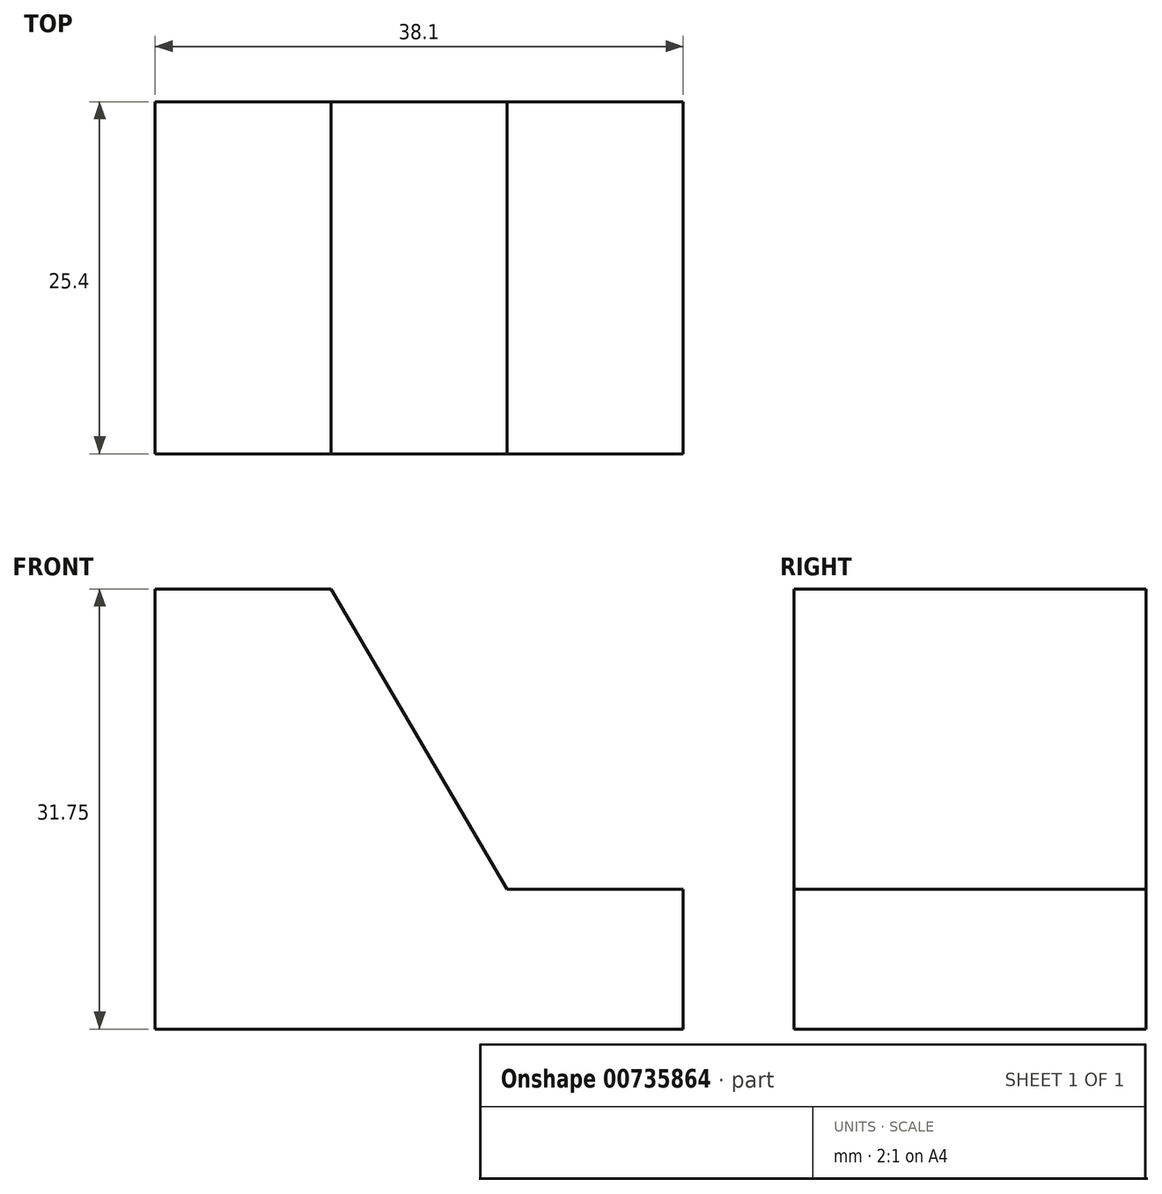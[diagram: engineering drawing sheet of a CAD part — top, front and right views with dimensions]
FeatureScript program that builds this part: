
annotation { "Feature Type Name" : "Feature", "Feature Type Description" : "" }
export const myFeature = defineFeature(function(context is Context, id is Id, definition is map)
    precondition{}
    {
        {
            var Q0;
            Q0=qCreatedBy(makeId("Front.planeOp"),FACE);
            var sketch = newSketch(context, id + "F0", { "sketchPlane" : qUnion([Q0])});
            skLineSegment(sketch, "E0", {"start": v(0, 0) * mm, "end": v(38.1, 0) * mm});
            skLineSegment(sketch, "E1", {"start": v(38.1, 0) * mm, "end": v(38.1, 31.75) * mm});
            skLineSegment(sketch, "E2", {"start": v(38.1, 31.75) * mm, "end": v(0, 31.75) * mm});
            skLineSegment(sketch, "E3", {"start": v(0, 31.75) * mm, "end": v(0, 0) * mm});
            skSolve(sketch);
        }
        {
            var Q0;
            Q0=makeQuery(id+"F0.imprint","IMPRINT",FACE,{"disambiguationData":[TD([[makeQuery(id+"F0.imprint","IMPRINT",EDGE,{"derivedFrom":sQuery(id+"F0.wireOp",EDGE,"E0")}),1.0]])]});
            extrude(context, id + "F1", {"entities" : qUnion([Q0]), "depth" : 25.4 * mm, "offsetDistance" : 25.4 * mm});
        }
        {
            var Q0;
            Q0=makeQuery(id+"F1.opExtrude","CAP_FACE",FACE,{"disambiguationData":[OSD([sQuery(id+"F0.wireOp",EDGE,"E0"),sQuery(id+"F0.wireOp",EDGE,"E1"),sQuery(id+"F0.wireOp",EDGE,"E2"),sQuery(id+"F0.wireOp",EDGE,"E3")])],"isStart":true});
            var sketch = newSketch(context, id + "F2", { "sketchPlane" : qUnion([Q0])});
            skLineSegment(sketch, "E4", {"start": v(-12.7, 31.75) * mm, "end": v(-25.4, 10.08) * mm});
            skLineSegment(sketch, "E5", {"start": v(-25.4, 10.08) * mm, "end": v(-38.1, 10.08) * mm});
            skSolve(sketch);
        }
        {
            var Q0;
            {var subQ0=sQuery(id+"F2.wireOp",EDGE,"E4");Q0=makeQuery(id+"F2.imprint","IMPRINT",FACE,{"disambiguationData":[TD([[makeQuery(id+"F2.imprint","IMPRINT",EDGE,{"derivedFrom":subQ0}),-1.0]])]});}
            extrude(context, id + "F3", {"entities" : qUnion([Q0]), "operationType" : NewBodyOperationType.REMOVE, "oppositeDirection" : true, "depth" : 25.4 * mm, "offsetDistance" : 25.4 * mm});
        }
    });
